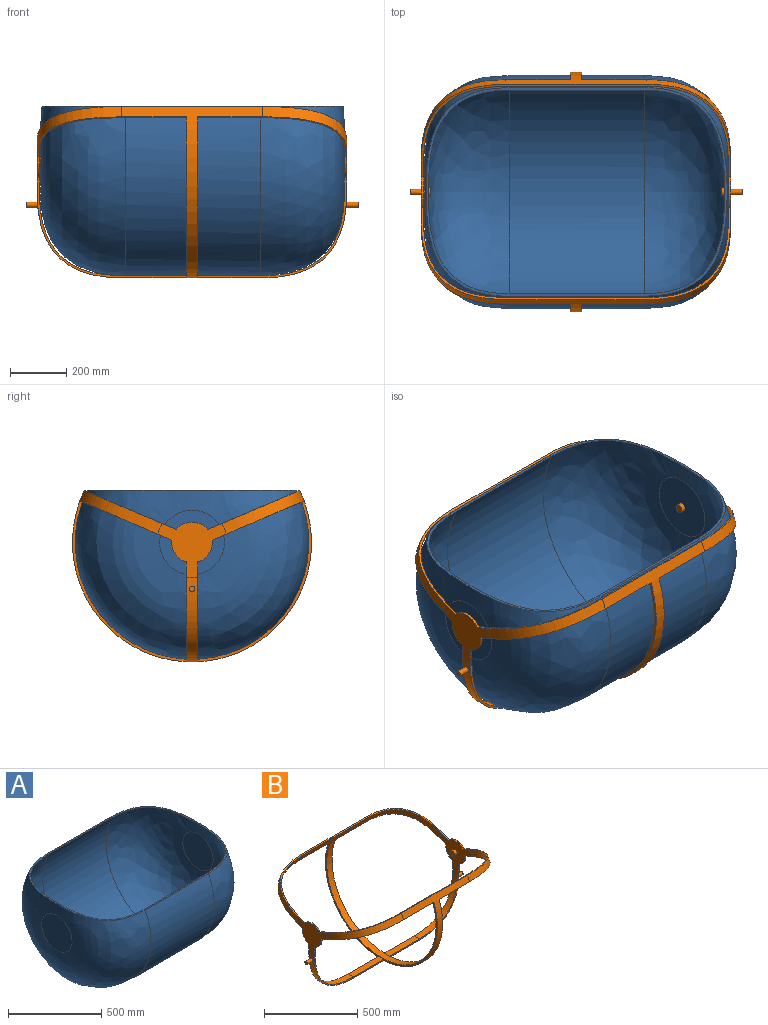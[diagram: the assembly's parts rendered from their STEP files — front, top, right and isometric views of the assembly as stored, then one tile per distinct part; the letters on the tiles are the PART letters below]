
ASSEMBLY  parts=2 mates=1
PART A: 11 faces, bbox 1096x846x846 mm
  f0: plane 1070.4x741.83mm, normal (0,0,1), area 27156.3mm2, adj f1,f4,f5,f6,f9,f10
  f1: cylinder r=415mm len=830mm, axis (-1,0,0), area 811107.2mm2, adj f0,f4,f5
  f2: plane 230.01x230.01mm, normal (1,0,0), area 41544.6mm2, adj f4
  f3: plane 230.01x230.01mm, normal (-1,0,0), area 41543.9mm2, adj f5
  f4: bspline ~830x830mm, area 679315.2mm2, adj f0,f1,f2
  f5: bspline ~830x830mm, area 679317.6mm2, adj f0,f1,f3
  f6: cylinder r=407mm len=814mm, axis (-1,0,0), area 799335.1mm2, adj f0,f9,f10
  f7: plane 230x230mm, normal (-1,0,0), area 41544.6mm2, adj f9
  f8: plane 230x230mm, normal (1,0,0), area 41543.9mm2, adj f10
  f9: offset ~846x846mm, area 654619.7mm2, adj f0,f6,f7
  f10: offset ~846x846mm, area 654530.8mm2, adj f0,f6,f8
PART B: 55 faces, bbox 1196x866x700.2 mm
  f0: offset ~317.62x316mm, area 18722.2mm2, adj f1,f2,f3,f52,f53,f54
  f1: cylinder r=10mm len=20mm, axis (-1,0,0), area 0mm2, adj f0,f2
  f2: plane 20x16.64mm, normal (-1,0,0), area 278.4mm2, adj f0,f1
  f3: plane 242.77x197.09mm, normal (-1,0,0), area 22007.4mm2, adj f0,f4,f6,f44,f45,f46,f47,f48
  f4: cylinder r=15mm len=30mm, axis (-1,0,0), area 2186.6mm2, adj f3,f5
  f5: plane 30x30mm, normal (-1,0,0), area 706.9mm2, adj f4
  f6: plane 530x326.92mm, normal (0,0.39,-0.92), area 6130.6mm2, adj f3,f7,f35,f40,f41,f43,f44,f51
  f7: cylinder r=417mm len=500mm, axis (-1,0,0), area 18429.4mm2, adj f6,f8,f32,f33,f34,f43,f44,f45
  f8: plane 530x326.92mm, normal (0,0.39,-0.92), area 6129mm2, adj f7,f9,f10,f28,f29,f32,f34,f41
  f9: bspline ~322.87x300mm, area 19497mm2, adj f8,f10,f41,f45
  f10: plane 243.1x197.08mm, normal (-1,0,0), area 22714.4mm2, adj f8,f9,f11,f12,f13,f18,f19,f24
  f11: cylinder r=72.06mm len=111.74mm, axis (1,0,0), area 1022.9mm2, adj f10,f29,f45,f47
  f12: bspline ~322.87x300mm, area 19497mm2, adj f10,f13,f41,f47
  f13: plane 530x326.93mm, normal (0,-0.39,-0.92), area 6129mm2, adj f10,f12,f14,f17,f18,f29,f32,f41
  f14: cylinder r=417mm len=500mm, axis (-1,0,0), area 18439.6mm2, adj f13,f15,f17,f32,f43,f47,f48,f49
  f15: plane 40x1.75mm, normal (0,0.48,0.88), area 80.1mm2, adj f14,f16,f32,f43
  f16: cylinder r=415mm len=830mm, axis (1,0,0), area 67041.4mm2, adj f15,f32,f33,f43
  f17: offset ~338.87x316mm, area 18993.9mm2, adj f13,f14,f29,f47
  f18: cylinder r=72.06mm len=77.93mm, axis (1,0,0), area 813.2mm2, adj f10,f13,f19,f29
  f19: plane 530.03x355.35mm, normal (0,-1,0), area 6129.2mm2, adj f10,f18,f20,f23,f24,f29,f32,f41
  f20: offset ~317.62x316mm, area 18717.8mm2, adj f19,f21,f22,f23,f27,f29
  f21: cylinder r=10mm len=20mm, axis (1,0,0), area 0mm2, adj f20,f22
  f22: plane 20x16.64mm, normal (1,0,0), area 278.4mm2, adj f20,f21
  f23: cylinder r=417mm len=230mm, axis (-1,0,0), area 9208.4mm2, adj f19,f20,f27,f32
  f24: bspline ~301.62x300mm, area 19185.1mm2, adj f10,f19,f25,f27,f41
  f25: cylinder r=10mm len=40.79mm, axis (1,0,0), area 2562.9mm2, adj f24,f26
  f26: plane 20x20mm, normal (-1,0,0), area 314.2mm2, adj f25
  f27: plane 530x355.29mm, normal (0,1,0), area 6128.9mm2, adj f10,f20,f23,f24,f28,f29,f32,f41
  f28: cylinder r=72.06mm len=77.94mm, axis (1,0,0), area 813.2mm2, adj f8,f10,f27,f29
  f29: plane 242.77x197.09mm, normal (1,0,0), area 22007.3mm2, adj f8,f11,f13,f17,f18,f19,f20,f27
  f30: cylinder r=15mm len=30mm, axis (-1,0,0), area 2186.6mm2, adj f29,f31
  f31: plane 30x30mm, normal (1,0,0), area 706.9mm2, adj f30
  f32: plane 850x605.56mm, normal (-1,0,0), area 16011mm2, adj f7,f8,f13,f14,f15,f16,f19,f23
  f33: plane 40x1.79mm, normal (0,-0.45,0.89), area 80mm2, adj f7,f16,f32,f43
  f34: offset ~338.87x316mm, area 18993.9mm2, adj f7,f8,f29,f45
  f35: plane 243.1x197.08mm, normal (1,0,0), area 22714.3mm2, adj f6,f36,f39,f40,f45,f46,f47,f49
  f36: bspline ~301.62x300mm, area 19189.9mm2, adj f35,f37,f41,f52,f54
  f37: cylinder r=10mm len=40.79mm, axis (-1,0,0), area 2562.9mm2, adj f36,f38
  f38: plane 20x20mm, normal (1,0,0), area 314.2mm2, adj f37
  f39: bspline ~322.87x300mm, area 19497.3mm2, adj f35,f41,f47,f49
  f40: bspline ~322.87x300mm, area 19497.3mm2, adj f6,f35,f41,f45
  f41: cylinder r=425mm len=850mm, axis (-1,0,0), area 123918.2mm2, adj f6,f8,f9,f12,f13,f19,f24,f27
  f42: plane 40.01x0.03mm, normal (0,0.48,0.88), area 1.2mm2, adj f41,f47
  f43: plane 850x605.56mm, normal (1,0,0), area 16011mm2, adj f6,f7,f14,f15,f16,f33,f41,f49
  f44: offset ~338.87x316mm, area 18994.8mm2, adj f3,f6,f7,f45
  f45: plane 1100x326.92mm, normal (0,-0.39,0.92), area 12580mm2, adj f3,f7,f9,f10,f11,f29,f34,f35
  f46: cylinder r=72.06mm len=111.74mm, axis (1,0,0), area 1022.9mm2, adj f3,f35,f45,f47
  f47: plane 1100.01x326.94mm, normal (0,0.39,0.92), area 12578.8mm2, adj f3,f10,f11,f12,f14,f17,f29,f35
  f48: offset ~338.87x316mm, area 18994.8mm2, adj f3,f14,f47,f49
  f49: plane 530x326.93mm, normal (0,-0.39,-0.92), area 6130.6mm2, adj f3,f14,f35,f39,f41,f43,f48,f50
  f50: cylinder r=72.06mm len=77.93mm, axis (1,0,0), area 813.2mm2, adj f3,f35,f49,f54
  f51: cylinder r=72.06mm len=77.94mm, axis (1,0,0), area 813.2mm2, adj f3,f6,f35,f52
  f52: plane 530x355.29mm, normal (0,1,0), area 6130.4mm2, adj f0,f3,f35,f36,f41,f43,f51,f53
  f53: cylinder r=417mm len=230mm, axis (-1,0,0), area 9208.4mm2, adj f0,f43,f52,f54
  f54: plane 530.03x355.35mm, normal (0,-1,0), area 6130.8mm2, adj f0,f3,f35,f36,f41,f43,f50,f53
PLACE A at identity fixed
PLACE B t=(-2,0,0)mm
MATE fastened A.f1 <-> B.f18  axis (1,0,0) through (540,0,0)mm
